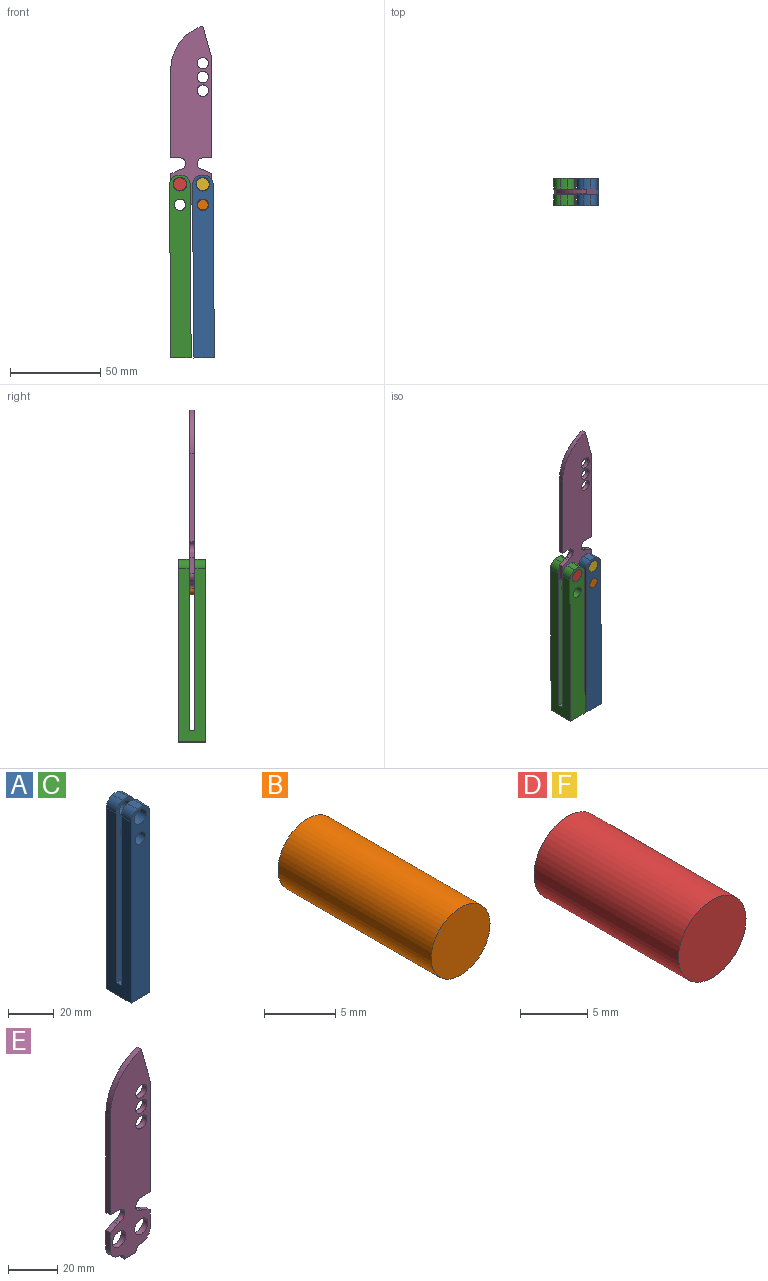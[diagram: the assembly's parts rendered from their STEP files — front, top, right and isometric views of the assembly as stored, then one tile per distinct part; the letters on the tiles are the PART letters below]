
ASSEMBLY  parts=6 mates=5
PART A: 18 faces, bbox 11.4x15.2x101.6 mm
  f0: plane 15.24x11.43mm, normal (0,0,-1), area 174.2mm2, adj f1,f2,f12,f13
  f1: plane 101.6x11.43mm, normal (0,1,0), area 1072.2mm2, adj f0,f7,f9,f11,f12,f13,f16,f17
  f2: plane 101.6x11.43mm, normal (0,-1,0), area 1072.2mm2, adj f0,f6,f8,f10,f12,f13,f14,f15
  f3: plane 95.25x11.43mm, normal (0,-1,0), area 999.6mm2, adj f5,f7,f9,f11,f12,f13,f16,f17
  f4: plane 95.25x11.43mm, normal (0,1,0), area 999.6mm2, adj f5,f6,f8,f10,f12,f13,f14,f15
  f5: plane 11.43x3.05mm, normal (0,0,1), area 34.8mm2, adj f3,f4,f12,f13
  f6: cylinder r=7.62mm len=6.1mm, axis (0,1,0), area 23.5mm2, adj f2,f4,f14,f15
  f7: cylinder r=7.62mm len=6.1mm, axis (0,-1,0), area 23.5mm2, adj f1,f3,f16,f17
  f8: cylinder r=3.81mm len=7.62mm, axis (0,-1,0), area 145.9mm2, adj f2,f4
  f9: cylinder r=3.81mm len=7.62mm, axis (0,-1,0), area 145.9mm2, adj f1,f3
  f10: cylinder r=3.17mm len=6.35mm, axis (0,-1,0), area 121.6mm2, adj f2,f4
  f11: cylinder r=3.17mm len=6.35mm, axis (0,-1,0), area 121.6mm2, adj f1,f3
  f12: plane 96.44x15.24mm, normal (1,0,0), area 1195.1mm2, adj f0,f1,f2,f3,f4,f5,f15,f17
  f13: plane 96.44x15.24mm, normal (-1,0,0), area 1195.1mm2, adj f0,f1,f2,f3,f4,f5,f14,f16
  f14: cylinder r=5.08mm len=6.1mm, axis (0,1,0), area 40.8mm2, adj f2,f4,f6,f13
  f15: cylinder r=5.08mm len=6.1mm, axis (0,1,0), area 40.8mm2, adj f2,f4,f6,f12
  f16: cylinder r=5.08mm len=6.1mm, axis (0,-1,0), area 40.8mm2, adj f1,f3,f7,f13
  f17: cylinder r=5.08mm len=6.1mm, axis (0,-1,0), area 40.8mm2, adj f1,f3,f7,f12
PART B: 3 faces, bbox 5.8x15.2x5.8 mm
  f0: cylinder r=2.92mm len=15.24mm, axis (0,-1,0), area 279.7mm2, adj f1,f2
  f1: plane 5.84x5.84mm, normal (0,1,0), area 26.8mm2, adj f0
  f2: plane 5.84x5.84mm, normal (0,-1,0), area 26.8mm2, adj f0
PART C: same geometry as A
PART D: 3 faces, bbox 7.1x15.2x7.1 mm
  f0: cylinder r=3.56mm len=15.24mm, axis (0,-1,0), area 340.5mm2, adj f1,f2
  f1: plane 7.11x7.11mm, normal (0,1,0), area 39.7mm2, adj f0
  f2: plane 7.11x7.11mm, normal (0,-1,0), area 39.7mm2, adj f0
PART E: 26 faces, bbox 22.9x2.5x99.3 mm
  f0: plane 8.89x2.54mm, normal (-1,0,0), area 22.6mm2, adj f2,f3,f16,f20
  f1: plane 8.89x2.54mm, normal (1,0,0), area 22.6mm2, adj f2,f3,f13,f19
  f2: plane 99.3x22.86mm, normal (0,1,0), area 1754.9mm2, adj f0,f1,f4,f5,f6,f7,f8,f9
  f3: plane 99.3x22.86mm, normal (0,-1,0), area 1754.9mm2, adj f0,f1,f4,f5,f6,f7,f8,f9
  f4: cylinder r=3.17mm len=3.18mm, axis (0,-1,0), area 12.7mm2, adj f2,f3,f12,f20
  f5: plane 49.02x2.54mm, normal (-1,0,0), area 124.5mm2, adj f2,f3,f15,f21
  f6: plane 55.11x2.54mm, normal (1,0,0), area 140mm2, adj f2,f3,f14,f22
  f7: cylinder r=3.81mm len=7.62mm, axis (0,-1,0), area 60.8mm2, adj f2,f3
  f8: cylinder r=3.81mm len=7.62mm, axis (0,-1,0), area 60.8mm2, adj f2,f3
  f9: cylinder r=3.17mm len=6.3mm, axis (0,-1,0), area 23.9mm2, adj f2,f3,f14,f17
  f10: cylinder r=3.17mm len=6.3mm, axis (0,-1,0), area 23.9mm2, adj f2,f3,f15,f18
  f11: cylinder r=3.17mm len=3.18mm, axis (0,-1,0), area 12.7mm2, adj f2,f3,f12,f19
  f12: plane 6.35x2.54mm, normal (0,0,-1), area 16.1mm2, adj f2,f3,f4,f11
  f13: plane 4.27x2.54mm, normal (0.45,0,0.89), area 12.1mm2, adj f1,f2,f3,f17
  f14: plane 5.08x2.54mm, normal (0,0,-1), area 12.9mm2, adj f2,f3,f6,f9
  f15: plane 5.08x2.54mm, normal (0,0,-1), area 12.9mm2, adj f2,f3,f5,f10
  f16: plane 4.27x2.54mm, normal (-0.45,0,0.89), area 12.1mm2, adj f0,f2,f3,f18
  f17: cylinder r=5.08mm len=2.54mm, axis (0,-1,0), area 3.7mm2, adj f2,f3,f9,f13
  f18: cylinder r=5.08mm len=2.54mm, axis (0,-1,0), area 3.7mm2, adj f2,f3,f10,f16
  f19: cylinder r=5.08mm len=5.08mm, axis (0,-1,0), area 20.3mm2, adj f1,f2,f3,f11
  f20: cylinder r=5.08mm len=5.08mm, axis (0,-1,0), area 20.3mm2, adj f0,f2,f3,f4
  f21: cylinder r=25.4mm len=24.25mm, axis (0,-1,0), area 81.8mm2, adj f2,f3,f5,f22
  f22: plane 18.15x5.03mm, normal (0.96,0,0.27), area 47.8mm2, adj f2,f3,f6,f21
  f23: cylinder r=3.17mm len=6.35mm, axis (0,-1,0), area 50.7mm2, adj f2,f3
  f24: cylinder r=3.17mm len=6.35mm, axis (0,-1,0), area 50.7mm2, adj f2,f3
  f25: cylinder r=3.17mm len=6.35mm, axis (0,-1,0), area 50.7mm2, adj f2,f3
PART F: same geometry as D
PLACE A rot(axis=(0,-1,0),0.4deg) t=(-35.91,-7.62,-82.75)mm
PLACE B rot(axis=(0,-1,0),0.4deg) t=(-28.91,-7.62,2.39)mm
PLACE C rot(axis=(0,-1,0),0.3deg) t=(-48.82,-7.62,-82.74)mm
PLACE D t=(-41.7,-7.62,13.82)mm
PLACE E t=(-46.78,-1.27,13.82)mm fixed
PLACE F t=(-29,-7.62,13.82)mm
MATE fastened D.f0 <-> E.f8  axis (0,-1,0) through (-41.7,0,13.82)mm
MATE fastened F.f0 <-> E.f7  axis (0,-1,0) through (-29,0,13.82)mm
MATE fastened B.f0 <-> A.f10  axis (0,-1,0) through (-28.91,-7.62,2.39)mm
MATE revolute A.f8 <-> F.f0  axis (0,-1,0) through (-29,-7.62,13.82)mm
MATE revolute C.f8 <-> D.f0  axis (0,-1,0) through (-41.7,-7.62,13.82)mm
